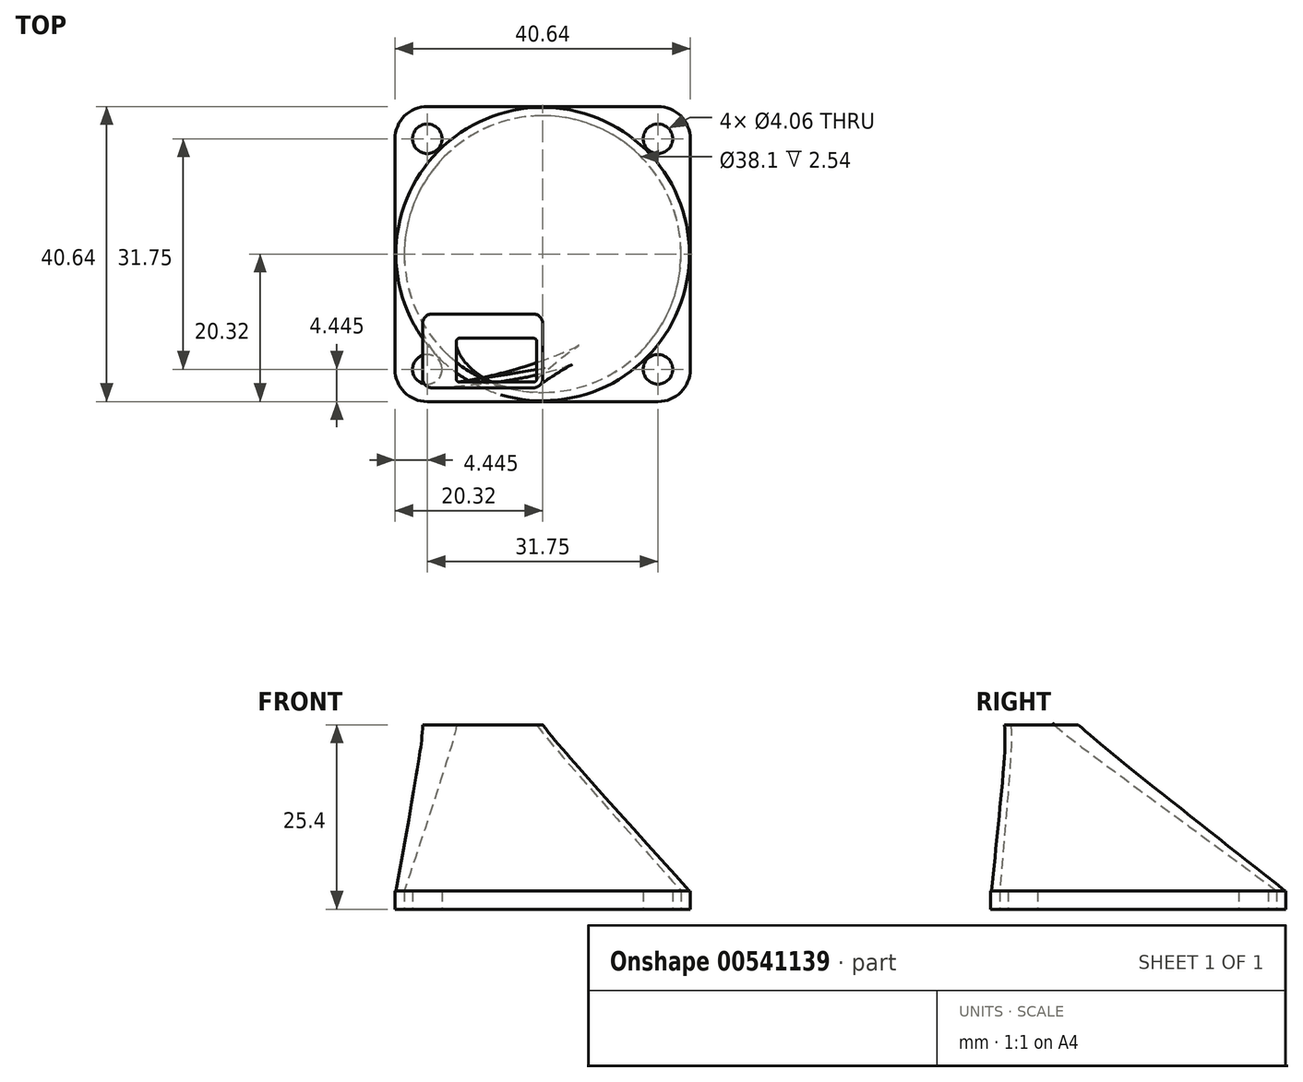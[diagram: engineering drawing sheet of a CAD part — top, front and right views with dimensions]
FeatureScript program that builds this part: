
annotation { "Feature Type Name" : "Feature", "Feature Type Description" : "" }
export const myFeature = defineFeature(function(context is Context, id is Id, definition is map)
    precondition{}
    {
        {
            var Q0;
            Q0=qCreatedBy(makeId("Top.planeOp"),FACE);
            var sketch = newSketch(context, id + "F0", { "sketchPlane" : qUnion([Q0])});
            skCircle(sketch, "E0", {"center": v(0, 0) * mm, "radius": 19.05 * mm});
            skLineSegment(sketch, "E1.bottom", {"start": v(-15.88, -20.32) * mm, "end": v(15.88, -20.32) * mm});
            skLineSegment(sketch, "E1.top", {"start": v(-15.88, 20.32) * mm, "end": v(15.88, 20.32) * mm});
            skLineSegment(sketch, "E1.left", {"start": v(-20.32, -15.87) * mm, "end": v(-20.32, 15.88) * mm});
            skLineSegment(sketch, "E1.right", {"start": v(20.32, -15.87) * mm, "end": v(20.32, 15.88) * mm});
            skPoint(sketch, "E2.visualSharp", {"position": v(-20.32, 20.32) * mm});
            skArc(sketch, "E2.filletArc", {"start": v(-15.88, 20.32) * mm, "mid": v(-19.02, 19.02) * mm, "end": v(-20.32, 15.88) * mm});
            skPoint(sketch, "E3.visualSharp", {"position": v(20.32, 20.32) * mm});
            skArc(sketch, "E3.filletArc", {"start": v(20.32, 15.88) * mm, "mid": v(19.02, 19.02) * mm, "end": v(15.88, 20.32) * mm});
            skPoint(sketch, "E4.visualSharp", {"position": v(20.32, -20.32) * mm});
            skArc(sketch, "E4.filletArc", {"start": v(15.88, -20.32) * mm, "mid": v(19.02, -19.02) * mm, "end": v(20.32, -15.87) * mm});
            skPoint(sketch, "E5.visualSharp", {"position": v(-20.32, -20.32) * mm});
            skArc(sketch, "E5.filletArc", {"start": v(-20.32, -15.87) * mm, "mid": v(-19.02, -19.02) * mm, "end": v(-15.88, -20.32) * mm});
            skCircle(sketch, "E6", {"center": v(-15.88, -15.87) * mm, "radius": 2.03 * mm});
            skCircle(sketch, "E7", {"center": v(-15.88, 15.88) * mm, "radius": 2.03 * mm});
            skCircle(sketch, "E8", {"center": v(15.88, 15.88) * mm, "radius": 2.03 * mm});
            skCircle(sketch, "E9", {"center": v(15.88, -15.87) * mm, "radius": 2.03 * mm});
            skSolve(sketch);
        }
        {
            var Q0;
            Q0=makeQuery(id+"F0.imprint","IMPRINT",FACE,{"disambiguationData":[TD([[makeQuery(id+"F0.imprint","IMPRINT",EDGE,{"derivedFrom":sQuery(id+"F0.wireOp",EDGE,"E0")}),-1.0]])]});
            extrude(context, id + "F1", {"entities" : qUnion([Q0]), "depth" : 2.54 * mm, "offsetDistance" : 25.4 * mm});
        }
        {
            var Q0;
            Q0=qCreatedBy(makeId("Top.planeOp"),FACE);
            cPlane(context, id + "F2", {"entities" : qUnion([Q0]), "cplaneType" : CPlaneType.OFFSET, "offset" : 25.4 * mm, "width" : 152.4 * mm, "height" : 152.4 * mm});
        }
        {
            var Q0;
            Q0=qCreatedBy(id+"F2.planeOp",FACE);
            var sketch = newSketch(context, id + "F3", { "sketchPlane" : qUnion([Q0])});
            skLineSegment(sketch, "E10.bottom", {"start": v(-15.24, -8.26) * mm, "end": v(-1.27, -8.26) * mm});
            skLineSegment(sketch, "E10.top", {"start": v(-15.24, -18.42) * mm, "end": v(-1.27, -18.42) * mm});
            skLineSegment(sketch, "E10.left", {"start": v(-16.51, -9.53) * mm, "end": v(-16.51, -17.15) * mm});
            skLineSegment(sketch, "E10.right", {"start": v(0, -9.53) * mm, "end": v(0, -17.15) * mm});
            skPoint(sketch, "E11.visualSharp", {"position": v(-16.51, -8.26) * mm});
            skArc(sketch, "E11.filletArc", {"start": v(-15.24, -8.26) * mm, "mid": v(-16.14, -8.63) * mm, "end": v(-16.51, -9.53) * mm});
            skPoint(sketch, "E12.visualSharp", {"position": v(0, -8.26) * mm});
            skArc(sketch, "E12.filletArc", {"start": v(0, -9.53) * mm, "mid": v(-0.37, -8.63) * mm, "end": v(-1.27, -8.26) * mm});
            skPoint(sketch, "E13.visualSharp", {"position": v(0, -18.42) * mm});
            skArc(sketch, "E13.filletArc", {"start": v(-1.27, -18.42) * mm, "mid": v(-0.37, -18.04) * mm, "end": v(0, -17.15) * mm});
            skPoint(sketch, "E14.visualSharp", {"position": v(-16.51, -18.42) * mm});
            skArc(sketch, "E14.filletArc", {"start": v(-16.51, -17.15) * mm, "mid": v(-16.14, -18.04) * mm, "end": v(-15.24, -18.42) * mm});
            skSolve(sketch);
        }
        {
            var Q0;
            Q0=makeQuery(id+"F1.opExtrude","CAP_FACE",FACE,{"disambiguationData":[OSD([sQuery(id+"F0.wireOp",EDGE,"E0"),sQuery(id+"F0.wireOp",EDGE,"E1.bottom"),sQuery(id+"F0.wireOp",EDGE,"E1.top"),sQuery(id+"F0.wireOp",EDGE,"E1.left"),sQuery(id+"F0.wireOp",EDGE,"E1.right"),sQuery(id+"F0.wireOp",EDGE,"E2.filletArc"),sQuery(id+"F0.wireOp",EDGE,"E3.filletArc"),sQuery(id+"F0.wireOp",EDGE,"E4.filletArc"),sQuery(id+"F0.wireOp",EDGE,"E5.filletArc"),sQuery(id+"F0.wireOp",EDGE,"E6"),sQuery(id+"F0.wireOp",EDGE,"E7"),sQuery(id+"F0.wireOp",EDGE,"E8"),sQuery(id+"F0.wireOp",EDGE,"E9")])],"isStart":false});
            cPlane(context, id + "F4", {"entities" : qUnion([Q0]), "cplaneType" : CPlaneType.OFFSET, "offset" : 0 * mm, "width" : 152.4 * mm, "height" : 152.4 * mm});
        }
        {
            var Q0;
            Q0=qCreatedBy(id+"F4.planeOp",FACE);
            var sketch = newSketch(context, id + "F5", { "sketchPlane" : qUnion([Q0])});
            skCircle(sketch, "E15", {"center": v(0, 0) * mm, "radius": 20.2 * mm});
            skSolve(sketch);
        }
        {
            var Q1;
            Q1=makeQuery(id+"F5.imprint","IMPRINT",FACE,{"disambiguationData":[TD([[makeQuery(id+"F5.imprint","IMPRINT",EDGE,{"derivedFrom":sQuery(id+"F5.wireOp",EDGE,"E15")}),1.0]])]});
            var Q2;
            Q2=makeQuery(id+"F3.imprint","IMPRINT",FACE,{"disambiguationData":[TD([[makeQuery(id+"F3.imprint","IMPRINT",EDGE,{"derivedFrom":sQuery(id+"F3.wireOp",EDGE,"E10.bottom")}),-1.0]])]});
            loft(context, id + "F6", {"operationType" : NewBodyOperationType.ADD, "sheetProfilesArray" : [{ "sheetProfileEntities" : qUnion([Q1]) }, { "sheetProfileEntities" : qUnion([Q2]) }]});
        }
        {
            var Q0;
            Q0=makeQuery(id+"F6.opLoft","CAP_FACE",FACE,{"disambiguationData":[OSD([makeQuery(id+"F3.imprint","IMPRINT",FACE,{"disambiguationData":[TD([[makeQuery(id+"F3.imprint","IMPRINT",EDGE,{"derivedFrom":sQuery(id+"F3.wireOp",EDGE,"E10.bottom")}),-1.0]])]})])],"isStart":true});
            var sketch = newSketch(context, id + "F7", { "sketchPlane" : qUnion([Q0])});
            skFitSpline(sketch, "E16.0", {"points": [v(-11.9, -12.07) * mm, v(-11.9, -13.76) * mm, v(-11.9, -15.45) * mm, v(-11.9, -17.14) * mm]});
            skFitSpline(sketch, "E16.1", {"points": [v(-11.43, -11.6) * mm, v(-11.5, -11.6) * mm, v(-11.61, -11.62) * mm, v(-11.77, -11.72) * mm, v(-11.86, -11.85) * mm, v(-11.9, -11.97) * mm, v(-11.9, -12.03) * mm, v(-11.9, -12.07) * mm]});
            skFitSpline(sketch, "E16.2", {"points": [v(-11.9, -17.14) * mm, v(-11.9, -17.2) * mm, v(-11.88, -17.33) * mm, v(-11.77, -17.49) * mm, v(-11.64, -17.57) * mm, v(-11.52, -17.6) * mm, v(-11.46, -17.62) * mm, v(-11.43, -17.62) * mm]});
            skFitSpline(sketch, "E16.3", {"points": [v(-1.27, -11.6) * mm, v(-4.66, -11.6) * mm, v(-8.04, -11.6) * mm, v(-11.43, -11.6) * mm]});
            skFitSpline(sketch, "E16.4", {"points": [v(-11.43, -17.62) * mm, v(-8.04, -17.62) * mm, v(-4.66, -17.62) * mm, v(-1.27, -17.62) * mm]});
            skFitSpline(sketch, "E16.5", {"points": [v(-1.27, -17.62) * mm, v(-1.2, -17.62) * mm, v(-1.09, -17.6) * mm, v(-0.93, -17.49) * mm, v(-0.84, -17.36) * mm, v(-0.8, -17.24) * mm, v(-0.8, -17.18) * mm, v(-0.8, -17.14) * mm]});
            skFitSpline(sketch, "E16.6", {"points": [v(-0.8, -17.14) * mm, v(-0.8, -15.45) * mm, v(-0.8, -13.76) * mm, v(-0.8, -12.07) * mm]});
            skFitSpline(sketch, "E16.7", {"points": [v(-0.8, -12.07) * mm, v(-0.8, -12) * mm, v(-0.82, -11.88) * mm, v(-0.93, -11.72) * mm, v(-1.06, -11.64) * mm, v(-1.18, -11.6) * mm, v(-1.24, -11.6) * mm, v(-1.27, -11.6) * mm]});
            skSolve(sketch);
        }
        {
            var Q1;
            Q1=makeQuery(id+"F6.boolean.opBoolean","SPLIT",FACE,{"disambiguationData":[TD([makeQuery(id+"F1.opExtrude","SWEPT_FACE",FACE,{"disambiguationData":[OSD([sQuery(id+"F0.wireOp",EDGE,"E0")])]})])],"derivedFrom":makeQuery(id+"F6.opLoft","CAP_FACE",FACE,{"disambiguationData":[OSD([makeQuery(id+"F5.imprint","IMPRINT",FACE,{"disambiguationData":[TD([[makeQuery(id+"F5.imprint","IMPRINT",EDGE,{"derivedFrom":sQuery(id+"F5.wireOp",EDGE,"E15")}),1.0]])]})])],"isStart":true})});
            var Q2;
            Q2=makeQuery(id+"F7.imprint","IMPRINT",FACE,{"disambiguationData":[TD([[makeQuery(id+"F7.imprint","IMPRINT",EDGE,{"derivedFrom":sQuery(id+"F7.wireOp",EDGE,"E16.0")}),1.0]])]});
            loft(context, id + "F8", {"operationType" : NewBodyOperationType.REMOVE, "sheetProfilesArray" : [{ "sheetProfileEntities" : qUnion([Q1]) }, { "sheetProfileEntities" : qUnion([Q2]) }]});
        }
    });
